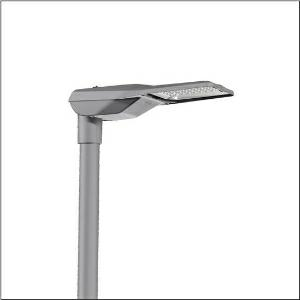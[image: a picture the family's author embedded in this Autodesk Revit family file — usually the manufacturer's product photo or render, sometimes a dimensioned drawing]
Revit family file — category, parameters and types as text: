
# Revit family: streetlight_sl_21_mini___st1_0a_5xe2d43s08jb_d214
name_source: partatom
category: Lighting Fixtures
units: mm (PartAtom-declared; Revit-internal decimal feet)

## family parameters
Cut with Voids When Loaded = No
Host = Face
Light Source = No
Part Type = Normal
Room Calculation Point = No
Round Connector Dimension = Use Diameter
Shared = No

## types (1)
- --- (1 x LED, 13500 lm, 88.6 W, 4000K)
    Apparent Load = 89 VA
    CIE Flux Codes = 40 73 97 100 100
    Color Rendering = 70
    Color Temperature = 4000K
    Default Elevation = 1800 mm
    Description = Streetlight SL 21 mini, mast luminaire, primary light control with lens, of PMMA, primary optical cover: cover, of toughened safety glass, transparent, light distribution: ST1.0a, light emission: direct distribution, primary light characteristic: asymmetric, installation type: side-entry, post-top, LED, High Power LED, rated luminous flux: 13.500lm, luminous efficacy: 152lm/W, light colour: 740, colour temperature: 4000K, control gear: D4i, control: overheat protection, constant luminous flux control, time-dependent luminous flux control, flexible luminous flux parameterisation, pre-setting: logarithmic dimming characteristic, mains connection: 220..240V, AC, 50/60Hz, start of lifetime: 89W, end of service life: 92W, reduction: 41W, luminaire housing, of diecast aluminium, powder-coated, Siteco® metallic grey (DB 702S), corrosivity category C5 mid according to DIN EN ISO 12944, please order mast flange separately, inclination adjustable: 0°, 5°, 10°, 15°, sealing non-destructively replaceable, multi-level sealing system, length: 628mm, width: 235mm, height: 110mm, mast flange for spigot size: 42mm (side-entry): 5XC10008XM4, 60/48mm (side-entry/post-top): 5XC10108XM2, 76/60mm (side-entry/post-top): 5XC10108XM1, mounting height: 4..8m, Smart Interface above, protection rating (complete): IP66, insulation class (complete): insulation class II (safety insulation), certification: CE, ENEC, ENEC+, VDE, impact resistance: IK10, permissible operating ambient temperature for outdoor applications: -40..+50°C, standard-compliant lighting for roads and squares, packaging unit: 1 piece

Light Distribution: ST1.0a
    Height = 110 mm
    Lamp = 1 x LED
    Lamp Light Flux = 13500 lm
    Lamp Power = 88.6 W
    Lamp count = 1
    Length = 625 mm
    Luminous efficacy = 152 lm/W
    Manufacturer = Siteco
    ModVariant = No
    Model = 5XE2D43S08JB
    Number of Poles = 1
    OnlyDefault = Yes
    Power Factor = 1
    Product Name = Streetlight SL 21 mini | ST1.0a
    Product group = mast luminaire | pylon top
    ProductGroupID = 6100
    Protection Class = Protection class II
    Protection Degree = IP 66
    RLX_Detail_Level = 1
    RLX_Emergency_Light_Flux = 0 lm
    RLX_Emergency_Type = 0
    RLX_Emergency_Type_DB = No
    RlxData = <blob elided: 26241 chars, md5=25e1a484>
    Socket = socket
    Standby Power = 0 W
    System Light Flux = 13500 lm
    System Power = 89 W
    Type Comments = factory setting: luminous flux: 100 % | dim-lin: 254 | 915 mA
    Type Image = l_1003515.jpg
    URL = http://relux.com
    VarID = @adj_011795
    Voltage = 0 V
    Weight = 0.00 kg
    Width = 234 mm

## geometry (parser evidence)
native form markers: Blend x4, Sweep x12
no freeform markers — native parametric forms only
